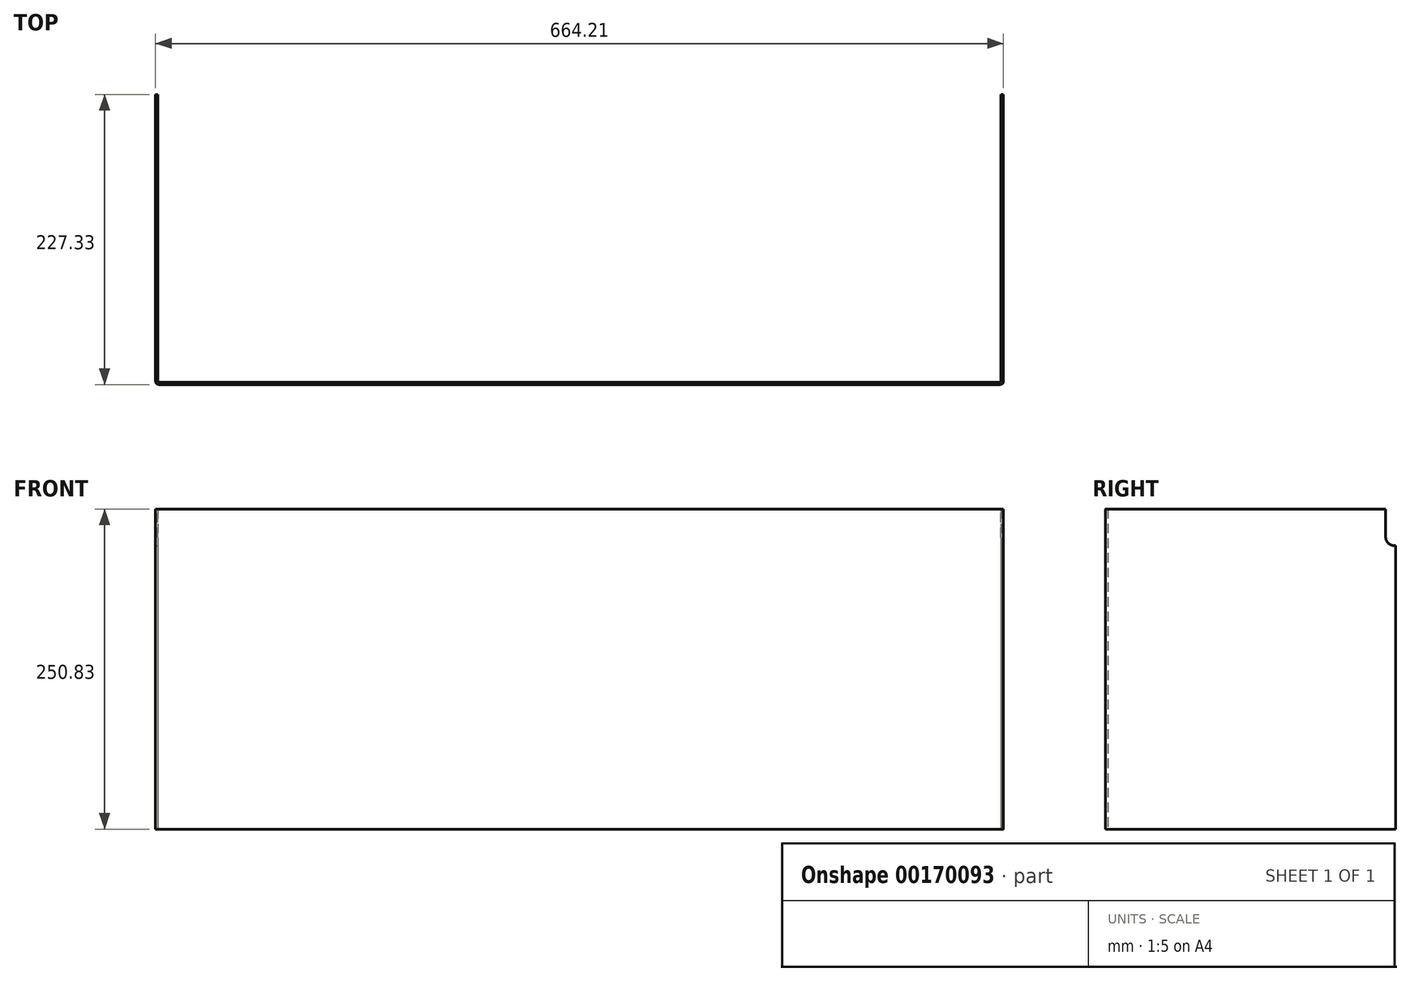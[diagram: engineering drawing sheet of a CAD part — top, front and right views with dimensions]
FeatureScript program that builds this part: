
annotation { "Feature Type Name" : "Feature", "Feature Type Description" : "" }
export const myFeature = defineFeature(function(context is Context, id is Id, definition is map)
    precondition{}
    {
        {
            var Q0;
            Q0=qCreatedBy(makeId("Top.planeOp"),FACE);
            var sketch = newSketch(context, id + "F0", { "sketchPlane" : qUnion([Q0])});
            skLineSegment(sketch, "E0.top", {"start": v(2.54, -227.33) * mm, "end": v(661.67, -227.33) * mm});
            skLineSegment(sketch, "E0.left", {"start": v(0, 0) * mm, "end": v(0, -224.79) * mm});
            skLineSegment(sketch, "E0.right", {"start": v(664.21, 0) * mm, "end": v(664.21, -224.79) * mm});
            skLineSegment(sketch, "E1.0", {"start": v(1.9, 0) * mm, "end": v(1.9, -225.43) * mm});
            skLineSegment(sketch, "E2.0", {"start": v(1.9, -225.43) * mm, "end": v(662.3, -225.43) * mm});
            skLineSegment(sketch, "E3.0", {"start": v(662.3, 0) * mm, "end": v(662.3, -225.43) * mm});
            skLineSegment(sketch, "E4.filletArc", {"start": v(662.3, -225.43) * mm, "end": v(662.3, -225.43) * mm});
            skLineSegment(sketch, "E5.filletArc", {"start": v(1.9, -225.43) * mm, "end": v(1.9, -225.43) * mm});
            skPoint(sketch, "E6.visualSharp", {"position": v(0, -227.33) * mm});
            skArc(sketch, "E6.filletArc", {"start": v(0, -224.79) * mm, "mid": v(0.74, -226.59) * mm, "end": v(2.54, -227.33) * mm});
            skPoint(sketch, "E7.visualSharp", {"position": v(664.21, -227.33) * mm});
            skArc(sketch, "E7.filletArc", {"start": v(661.67, -227.33) * mm, "mid": v(663.47, -226.59) * mm, "end": v(664.21, -224.79) * mm});
            skLineSegment(sketch, "E8", {"start": v(664.21, 0) * mm, "end": v(662.3, 0) * mm});
            skLineSegment(sketch, "E9", {"start": v(1.9, 0) * mm, "end": v(0, 0) * mm});
            skSolve(sketch);
        }
        {
            var Q0;
            Q0 = qSketchRegion(id + "F0", true);
            extrude(context, id + "F1", {"entities" : qUnion([Q0]), "depth" : 250.82 * mm});
        }
        {
            var Q0;
            Q0=makeQuery(id+"F1.opExtrude","SWEPT_FACE",FACE,{"disambiguationData":[OSD([sQuery(id+"F0.wireOp",EDGE,"E0.right")])]});
            var sketch = newSketch(context, id + "F2", { "sketchPlane" : qUnion([Q0])});
            skLineSegment(sketch, "E10.top", {"start": v(-1.57, 222.25) * mm, "end": v(0, 222.25) * mm});
            skLineSegment(sketch, "E11", {"start": v(-7.92, 228.6) * mm, "end": v(-7.92, 250.83) * mm});
            skLineSegment(sketch, "E12", {"start": v(-7.92, 250.83) * mm, "end": v(0, 250.83) * mm});
            skLineSegment(sketch, "E13", {"start": v(0, 250.83) * mm, "end": v(0, 222.25) * mm});
            skPoint(sketch, "E14.visualSharp", {"position": v(-7.92, 222.25) * mm});
            skArc(sketch, "E14.filletArc", {"start": v(-7.92, 228.6) * mm, "mid": v(-6.06, 224.1) * mm, "end": v(-1.57, 222.25) * mm});
            skSolve(sketch);
        }
        {
            var Q0;
            Q0 = qSketchRegion(id + "F2", true);
            extrude(context, id + "F3", {"entities" : qUnion([Q0]), "operationType" : NewBodyOperationType.REMOVE, "endBound" : BoundingType.THROUGH_ALL, "oppositeDirection" : true, "depth" : 25.4 * mm});
        }
    });
